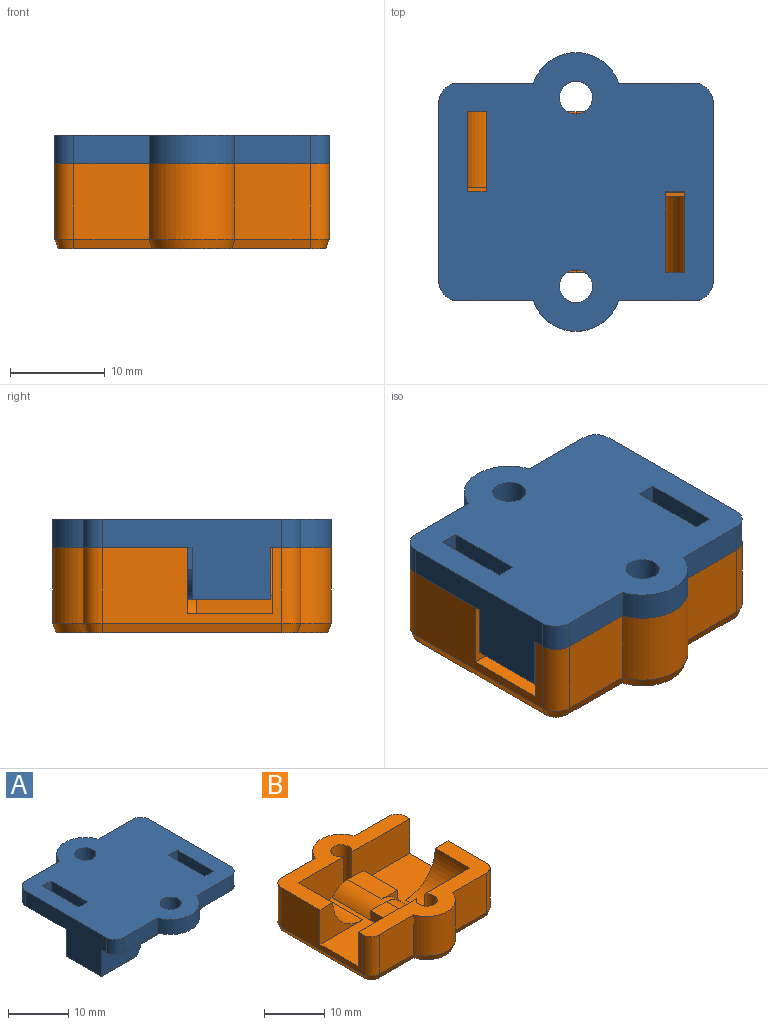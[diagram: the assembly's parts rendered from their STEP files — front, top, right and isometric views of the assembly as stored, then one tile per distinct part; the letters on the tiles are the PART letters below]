
ASSEMBLY  parts=2 mates=1
PART A: 42 faces, bbox 29x29.4x8.5 mm
  f0: plane 0.67x0.03mm, normal (0,0,1), area 0mm2, adj f11,f34
  f1: plane 8.5x8.35mm, normal (0,1,0), area 37.9mm2, adj f8,f9,f10,f14,f22,f35,f39,f40
  f2: plane 5.04x1.94mm, normal (0,1,0), area 4.7mm2, adj f4,f5,f6,f7,f17
  f3: plane 0.67x0.03mm, normal (0,0,1), area 0mm2, adj f20,f38
  f4: cylinder r=5.5mm len=8.25mm, axis (0,-1,0), area 51.8mm2, adj f2,f5,f11,f12,f41
  f5: plane 8.25x0.22mm, normal (0,0,-1), area 1.9mm2, adj f2,f4,f6,f11
  f6: cylinder r=7.66mm len=8.25mm, axis (0,-1,0), area 38.4mm2, adj f2,f5,f7,f11
  f7: plane 16.5x10.28mm, normal (0,0,-1), area 85.7mm2, adj f2,f6,f8,f11,f16,f17,f19,f20
  f8: plane 8.25x1.94mm, normal (0.86,0,-0.51), area 18.6mm2, adj f1,f7,f9,f11,f19
  f9: plane 8.25x8.2mm, normal (0,0,-1), area 67.7mm2, adj f1,f8,f10,f11
  f10: plane 19x8.5mm, normal (-1,0,0), area 102.4mm2, adj f1,f9,f11,f21,f22,f29,f30,f39
  f11: plane 23.97x5.5mm, normal (0,-1,0), area 110.9mm2, adj f0,f4,f5,f6,f7,f8,f9,f10
  f12: plane 9.34x8.5mm, normal (0,-1,0), area 38mm2, adj f4,f13,f17,f18,f21,f37,f39,f41
  f13: plane 19x8.5mm, normal (1,0,0), area 102.4mm2, adj f12,f18,f20,f21,f22,f24,f25,f39
  f14: cylinder r=5.5mm len=8.25mm, axis (0,1,0), area 51.8mm2, adj f1,f15,f19,f20,f40
  f15: plane 8.25x0.12mm, normal (0,0,-1), area 1mm2, adj f14,f16,f19,f20
  f16: cylinder r=5.89mm len=8.25mm, axis (0,1,0), area 40.6mm2, adj f7,f15,f19,f20
  f17: plane 8.25x1.94mm, normal (-1,0,0), area 16mm2, adj f2,f7,f12,f18,f20
  f18: plane 9.34x8.25mm, normal (0,0,-1), area 77.1mm2, adj f12,f13,f17,f20
  f19: plane 6.14x1.94mm, normal (0,-1,0), area 5.1mm2, adj f7,f8,f14,f15,f16
  f20: plane 23.97x5.5mm, normal (0,1,0), area 111.5mm2, adj f3,f7,f13,f14,f15,f16,f17,f18
  f21: plane 28.97x14.72mm, normal (0,0,-1), area 128.3mm2, adj f10,f11,f12,f13,f24,f30,f31,f32
  f22: plane 28.97x14.72mm, normal (0,0,-1), area 128.3mm2, adj f1,f10,f13,f20,f23,f25,f26,f27
  f23: plane 3x2mm, normal (0,-1,0), area 6mm2, adj f22,f35,f39,f40
  f24: cylinder r=2mm len=3mm, axis (0,0,-1), area 9.4mm2, adj f13,f21,f36,f39
  f25: cylinder r=2mm len=3mm, axis (0,0,-1), area 9.4mm2, adj f13,f22,f26,f39
  f26: plane 7.99x3mm, normal (0,1,0), area 24mm2, adj f22,f25,f27,f39
  f27: cylinder r=4.75mm len=9mm, axis (0,0,-1), area 35.4mm2, adj f22,f26,f28,f39
  f28: plane 7.99x3mm, normal (0,1,0), area 24mm2, adj f22,f27,f29,f39
  f29: cylinder r=2mm len=3mm, axis (0,0,-1), area 9.4mm2, adj f10,f22,f28,f39
  f30: cylinder r=2mm len=3mm, axis (0,0,-1), area 9.4mm2, adj f10,f21,f31,f39
  f31: plane 7.99x3mm, normal (0,-1,0), area 24mm2, adj f21,f30,f32,f39
  f32: cylinder r=4.75mm len=9mm, axis (0,0,-1), area 35.4mm2, adj f21,f31,f36,f39
  f33: plane 3x2mm, normal (0,1,0), area 6mm2, adj f21,f37,f39,f41
  f34: cylinder r=1.75mm len=3.5mm, axis (0,0,-1), area 33mm2, adj f0,f21,f39
  f35: plane 8.5x3mm, normal (1,0,0), area 25.5mm2, adj f1,f22,f23,f39
  f36: plane 7.99x3mm, normal (0,-1,0), area 24mm2, adj f21,f24,f32,f39
  f37: plane 8.5x3mm, normal (-1,0,0), area 25.5mm2, adj f12,f21,f33,f39
  f38: cylinder r=1.75mm len=3.5mm, axis (0,0,-1), area 33mm2, adj f3,f22,f39
  f39: plane 29.44x28.97mm, normal (0,0,1), area 652mm2, adj f1,f10,f12,f13,f23,f24,f25,f26
  f40: plane 8.5x5.29mm, normal (-1,0,0), area 44.4mm2, adj f1,f14,f20,f22,f23,f39
  f41: plane 8.5x5.29mm, normal (1,0,0), area 44.4mm2, adj f4,f11,f12,f21,f33,f39
PART B: 54 faces, bbox 29x29.5x9 mm
  f0: plane 17x10.84mm, normal (0,0,1), area 104.3mm2, adj f1,f10,f16,f18,f19,f30,f34
  f1: plane 13.53x7mm, normal (0,1,0), area 89.5mm2, adj f0,f5,f10,f17,f34,f35
  f2: plane 10.53x7mm, normal (0,1,0), area 60.5mm2, adj f3,f5,f17,f20,f36
  f3: plane 17x10.84mm, normal (0,0,1), area 104.3mm2, adj f2,f6,f14,f20,f21,f28,f30,f36
  f4: plane 28.97x14.22mm, normal (0,0,1), area 121.1mm2, adj f6,f7,f8,f9,f10,f14,f15,f16
  f5: plane 28.97x14.22mm, normal (0,0,1), area 121.1mm2, adj f1,f2,f6,f10,f11,f12,f13,f17
  f6: plane 19x8mm, normal (1,0,0), area 89mm2, adj f3,f4,f5,f14,f21,f24,f25,f44
  f7: plane 8x7.99mm, normal (0,1,0), area 63.9mm2, adj f4,f8,f25,f48
  f8: cylinder r=4.75mm len=9mm, axis (0,0,-1), area 94.5mm2, adj f4,f7,f9,f50
  f9: plane 8x7.99mm, normal (0,1,0), area 63.9mm2, adj f4,f8,f26,f51
  f10: plane 19x8mm, normal (-1,0,0), area 89mm2, adj f0,f1,f4,f5,f19,f23,f26,f47
  f11: plane 8x7.99mm, normal (0,-1,0), area 63.9mm2, adj f5,f12,f23,f43
  f12: cylinder r=4.75mm len=9mm, axis (0,0,-1), area 94.5mm2, adj f5,f11,f13,f41
  f13: plane 8x7.99mm, normal (0,-1,0), area 63.9mm2, adj f5,f12,f24,f40
  f14: plane 13.53x7mm, normal (0,-1,0), area 89.5mm2, adj f3,f4,f6,f15,f28,f29
  f15: cylinder r=1.75mm len=8mm, axis (0,0,-1), area 73.9mm2, adj f4,f14,f16,f27,f32,f53
  f16: plane 10.53x7mm, normal (0,-1,0), area 60.1mm2, adj f0,f4,f15,f18,f30
  f17: cylinder r=1.75mm len=8mm, axis (0,0,-1), area 73.9mm2, adj f1,f2,f5,f33,f38,f52
  f18: cylinder r=7mm len=8mm, axis (0,1,0), area 88mm2, adj f0,f4,f16,f19
  f19: plane 10x7mm, normal (0,-1,0), area 31.5mm2, adj f0,f4,f10,f18
  f20: cylinder r=7mm len=8mm, axis (0,-1,0), area 88mm2, adj f2,f3,f5,f21
  f21: plane 10x7mm, normal (0,1,0), area 31.5mm2, adj f3,f5,f6,f20
  f22: plane 28.71x28.24mm, normal (0,0,-1), area 638.9mm2, adj f40,f41,f42,f43,f44,f45,f46,f47
  f23: cylinder r=2mm len=8mm, axis (0,0,-1), area 25.1mm2, adj f5,f10,f11,f45
  f24: cylinder r=2mm len=8mm, axis (0,0,-1), area 25.1mm2, adj f5,f6,f13,f42
  f25: cylinder r=2mm len=8mm, axis (0,0,-1), area 25.1mm2, adj f4,f6,f7,f46
  f26: cylinder r=2mm len=8mm, axis (0,0,-1), area 25.1mm2, adj f4,f9,f10,f49
  f27: plane 1.91x0.28mm, normal (0,0,-1), area 0.4mm2, adj f15,f32
  f28: plane 8x1.94mm, normal (1,0,0), area 15.5mm2, adj f3,f14,f29,f31
  f29: plane 8x3.64mm, normal (0,0,1), area 29.1mm2, adj f14,f28,f30,f31,f32
  f30: cylinder r=4.39mm len=9mm, axis (0,1,0), area 43mm2, adj f0,f3,f16,f29,f31,f32,f37,f39
  f31: plane 3.64x1.94mm, normal (0,-1,0), area 2.1mm2, adj f28,f29,f30
  f32: plane 1.94x1.91mm, normal (0,1,0), area 3.7mm2, adj f15,f27,f29,f30
  f33: plane 1.91x0.28mm, normal (0,0,-1), area 0.4mm2, adj f17,f38
  f34: plane 8x1.94mm, normal (-1,0,0), area 15.5mm2, adj f0,f1,f35,f37
  f35: plane 8x3.64mm, normal (0,0,1), area 29.1mm2, adj f1,f34,f36,f37,f38
  f36: cylinder r=6.16mm len=8mm, axis (0,-1,0), area 33.7mm2, adj f2,f3,f35,f38,f39
  f37: plane 3.64x1.94mm, normal (0,1,0), area 2.1mm2, adj f30,f34,f35
  f38: plane 1.94x1.91mm, normal (0,-1,0), area 3.6mm2, adj f17,f33,f35,f36
  f39: plane 3.64x1.94mm, normal (0,-1,0), area 0.5mm2, adj f30,f36
  f40: plane 8.26x1.01mm, normal (0,-0.94,-0.34), area 8.6mm2, adj f13,f22,f41,f42
  f41: cone r=4.39mm half-angle=20deg, axis (0,0,1), area 12.4mm2, adj f12,f22,f40,f43
  f42: cone r=1.64mm half-angle=20deg, axis (0,0,1), area 3mm2, adj f22,f24,f40,f44
  f43: plane 8.26x1.01mm, normal (0,-0.94,-0.34), area 8.6mm2, adj f11,f22,f41,f45
  f44: plane 19x1mm, normal (0.94,0,-0.34), area 20.2mm2, adj f6,f22,f42,f46
  f45: cone r=1.64mm half-angle=20deg, axis (0,0,1), area 3mm2, adj f22,f23,f43,f47
  f46: cone r=1.64mm half-angle=20deg, axis (0,0,1), area 3mm2, adj f22,f25,f44,f48
  f47: plane 19x1mm, normal (-0.94,0,-0.34), area 20.2mm2, adj f10,f22,f45,f49
  f48: plane 8.26x1.01mm, normal (0,0.94,-0.34), area 8.6mm2, adj f7,f22,f46,f50
  f49: cone r=1.64mm half-angle=20deg, axis (0,0,1), area 3mm2, adj f22,f26,f47,f51
  f50: cone r=4.39mm half-angle=20deg, axis (0,0,1), area 12.4mm2, adj f8,f22,f48,f51
  f51: plane 8.26x1.01mm, normal (0,0.94,-0.34), area 8.6mm2, adj f9,f22,f49,f50
  f52: cone r=1.75mm half-angle=20deg, axis (0,0,-1), area 12.9mm2, adj f17,f22
  f53: cone r=1.75mm half-angle=20deg, axis (0,0,-1), area 12.9mm2, adj f15,f22
PLACE A t=(0.41,10.15,7.69)mm
PLACE B t=(0.41,10.15,7.69)mm
MATE fastened B.f12 <-> A.f32  axis (0,0,1) through (-0.18,-1.11,14.69)mm
